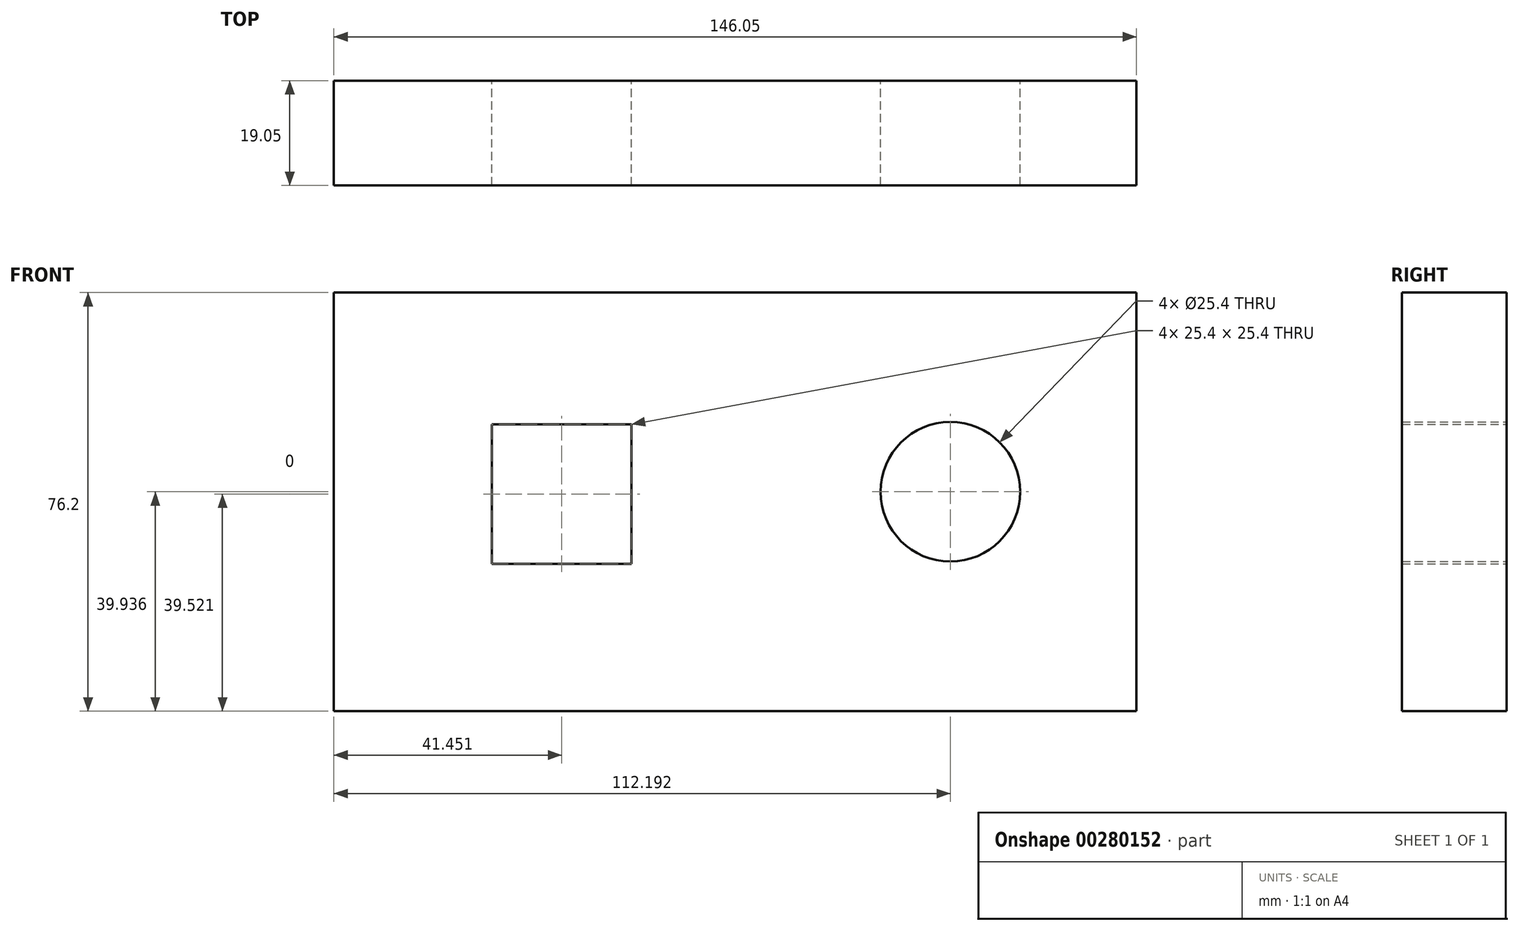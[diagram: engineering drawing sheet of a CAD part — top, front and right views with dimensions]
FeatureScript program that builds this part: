
annotation { "Feature Type Name" : "Feature", "Feature Type Description" : "" }
export const myFeature = defineFeature(function(context is Context, id is Id, definition is map)
    precondition{}
    {
        {
            var Q0;
            Q0=qCreatedBy(makeId("Front.planeOp"),FACE);
            var sketch = newSketch(context, id + "F0", { "sketchPlane" : qUnion([Q0])});
            skLineSegment(sketch, "E0.bottom", {"start": v(0, 0) * mm, "end": v(-146.05, 0) * mm});
            skLineSegment(sketch, "E0.top", {"start": v(0, 76.2) * mm, "end": v(-146.05, 76.2) * mm});
            skLineSegment(sketch, "E0.left", {"start": v(0, 0) * mm, "end": v(0, 76.2) * mm});
            skLineSegment(sketch, "E0.right", {"start": v(-146.05, 0) * mm, "end": v(-146.05, 76.2) * mm});
            skCircle(sketch, "E1", {"center": v(-33.86, 39.94) * mm, "radius": 12.7 * mm});
            skLineSegment(sketch, "E2.bottom", {"start": v(-117.3, 52.22) * mm, "end": v(-91.9, 52.22) * mm});
            skLineSegment(sketch, "E2.top", {"start": v(-117.3, 26.82) * mm, "end": v(-91.9, 26.82) * mm});
            skLineSegment(sketch, "E2.left", {"start": v(-117.3, 52.22) * mm, "end": v(-117.3, 26.82) * mm});
            skLineSegment(sketch, "E2.right", {"start": v(-91.9, 52.22) * mm, "end": v(-91.9, 26.82) * mm});
            skSolve(sketch);
        }
        {
            var Q0;
            Q0 = qSketchRegion(id + "F0", true);
            extrude(context, id + "F1", {"entities" : qUnion([Q0]), "depth" : 19.05 * mm});
        }
    });
